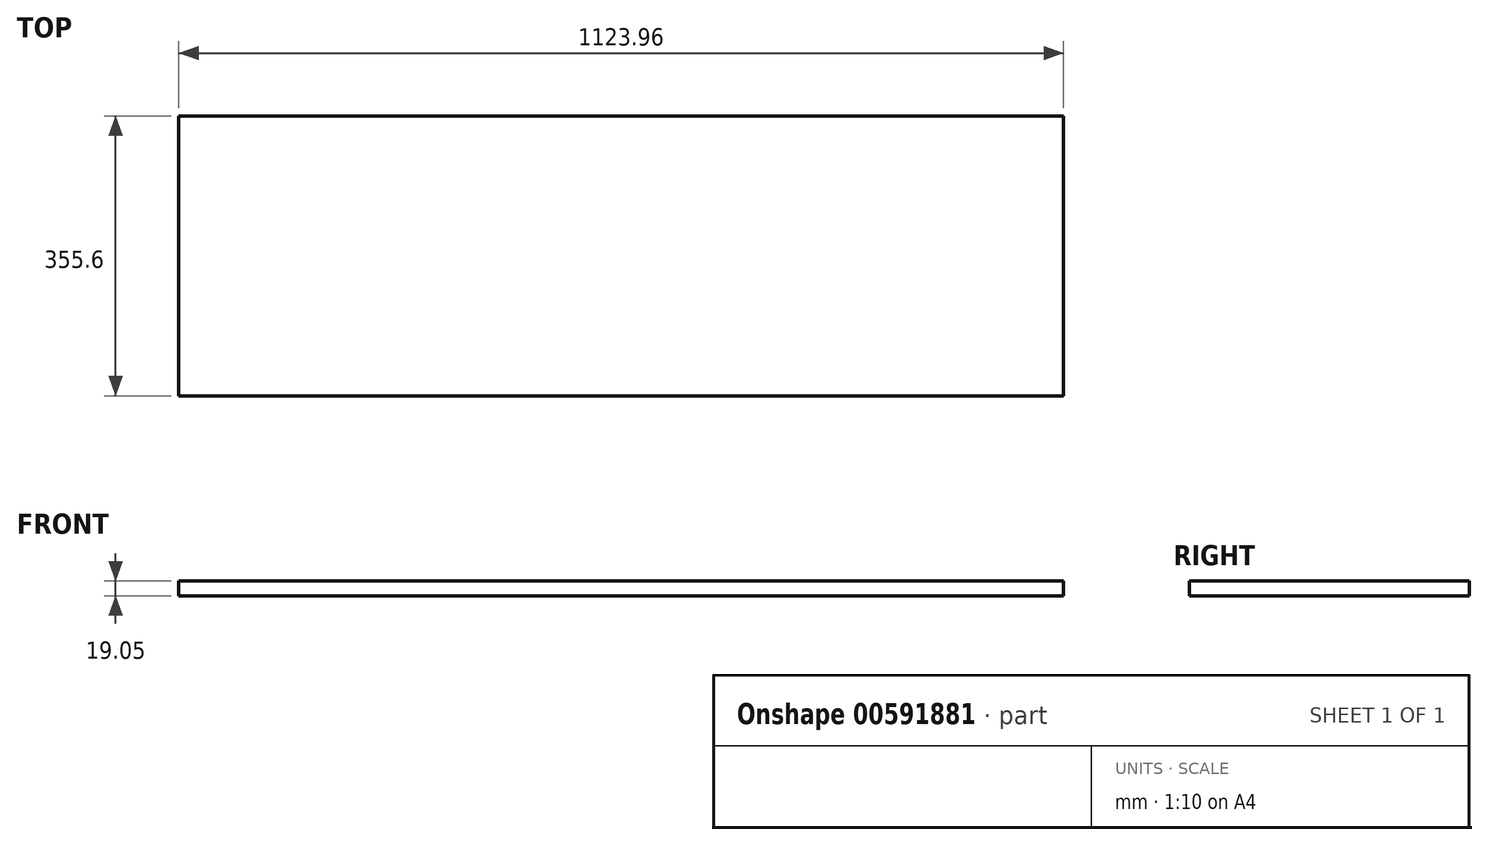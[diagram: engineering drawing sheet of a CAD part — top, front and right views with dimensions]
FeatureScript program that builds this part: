
annotation { "Feature Type Name" : "Feature", "Feature Type Description" : "" }
export const myFeature = defineFeature(function(context is Context, id is Id, definition is map)
    precondition{}
    {
        {
            var Q0;
            Q0=qCreatedBy(makeId("Top.planeOp"),FACE);
            var sketch = newSketch(context, id + "F0", { "sketchPlane" : qUnion([Q0])});
            skLineSegment(sketch, "E0.bottom", {"start": v(561.97, 177.8) * mm, "end": v(-561.98, 177.8) * mm});
            skLineSegment(sketch, "E0.top", {"start": v(561.98, -177.8) * mm, "end": v(-561.98, -177.8) * mm});
            skLineSegment(sketch, "E0.left", {"start": v(561.98, 177.8) * mm, "end": v(561.98, -177.8) * mm});
            skLineSegment(sketch, "E0.right", {"start": v(-561.98, 177.8) * mm, "end": v(-561.98, -177.8) * mm});
            skPoint(sketch, "E0.middle", {"position": v(0, 0) * mm});
            skSolve(sketch);
        }
        {
            var Q0;
            Q0=makeQuery(id+"F0.imprint","IMPRINT",FACE,{"disambiguationData":[TD([[makeQuery(id+"F0.imprint","IMPRINT",EDGE,{"derivedFrom":sQuery(id+"F0.wireOp",EDGE,"E0.bottom")}),1.0]])]});
            extrude(context, id + "F1", {"entities" : qUnion([Q0]), "depth" : 19.05 * mm, "offsetDistance" : 25.4 * mm});
        }
    });
